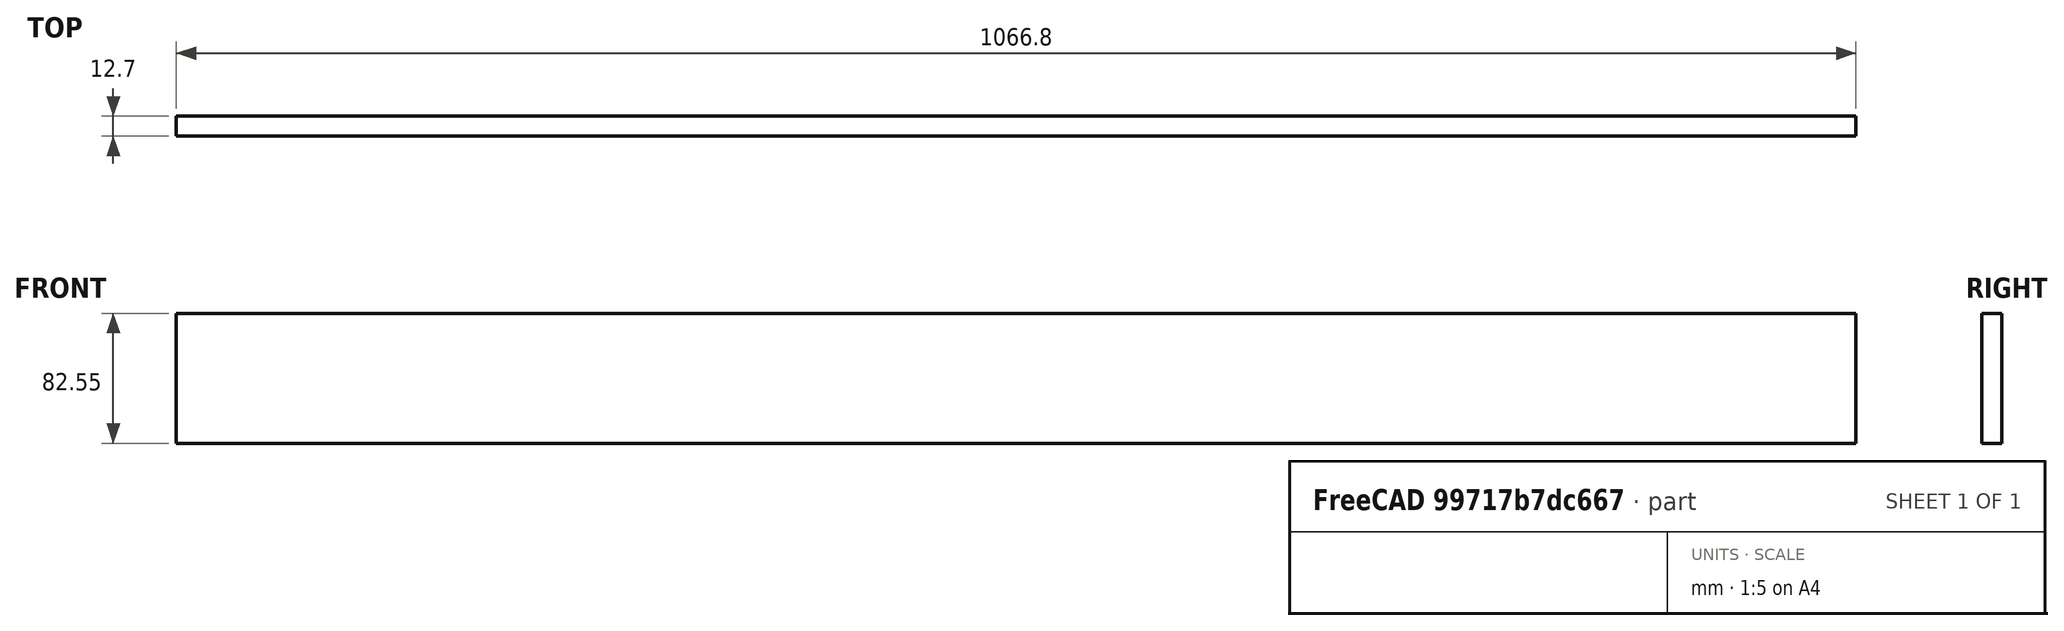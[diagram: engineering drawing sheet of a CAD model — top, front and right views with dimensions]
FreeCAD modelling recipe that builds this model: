
FCSTD DOCUMENT  (FreeCAD 0.21R33771 (Git))
Label: door
License: All rights reserved
LicenseURL: http://en.wikipedia.org/wiki/All_rights_reserved
objects: Sketcher::SketchObject×1, PartDesign::Pad×1, PartDesign::Body×1
note: 4 computed .brp shape members not serialized (recipe doc carries the construction recipe); baked Part::Feature solids carry a one-line shape summary decoded from their .brp
EXTERNAL_REF file=enclosure-dims.FCStd obj=Spreadsheet

FEATURE [Sketcher::SketchObject] Sketch  label="s-door"
  FullyConstrained = true
  MapMode = 5
  Placement = pos=(0,0,0) rot=(1,0,0;1.5708rad)
  Support = -> [XZ_Plane]
  expr: Constraints[13] = <<enclosure-dims>>#<<Spreadsheet>>.floor_t
  expr: Constraints[14] = <<enclosure-dims>>#<<Spreadsheet>>.door_h
  expr: Constraints[9] = <<enclosure-dims>>#<<Spreadsheet>>.floor_w
  sketch-geometry (5):
    g0: LineSegment StartX=-533.4 StartY=82.55 StartZ=0 EndX=533.4 EndY=82.55 EndZ=0
    g1: LineSegment StartX=533.4 StartY=82.55 StartZ=0 EndX=533.4 EndY=0 EndZ=0
    g2: LineSegment StartX=533.4 StartY=0 StartZ=0 EndX=-533.4 EndY=-1e-16 EndZ=0
    g3: LineSegment StartX=-533.4 StartY=-1e-16 StartZ=0 EndX=-533.4 EndY=82.55 EndZ=0
    g4: LineSegment StartX=-533.4 StartY=19.05 StartZ=0 EndX=533.4 EndY=19.05 EndZ=0
  constraints (15):
    c: Coincident(g0,g1)
    c: Coincident(g1,g2)
    c: Coincident(g2,g3)
    c: Coincident(g3,g0)
    c: Horizontal(g0)
    c: Vertical(g1)
    c: Vertical(g3)
    c: PointOnObject(g1,g-1)
    c: Symmetric(g2,g1,g-2)
    c: DistanceX(g0,g0) = 1066.8
    c: Horizontal(g4)
    c: PointOnObject(g4,g1)
    c: PointOnObject(g4,g3)
    c: DistanceY(g2,g4) = 19.05
    c: DistanceY(g4,g0) = 63.5
FEATURE [PartDesign::Pad] Pad
  Direction = (0,-1,-2e-16)
  Length = 12.7
  Length2 = 10
  Placement = pos=(0,0,0) rot=(1,0,0;1.5708rad)
  Profile = -> Sketch
  ReferenceAxis = -> Sketch [N_Axis]
  Type = 0
  expr: Length = <<enclosure-dims>>#<<Spreadsheet>>.wall_t
FEATURE [PartDesign::Body] Body  label="door"
  Group = -> [Sketch,Pad]
  Origin = -> Origin
  Tip = -> Pad
